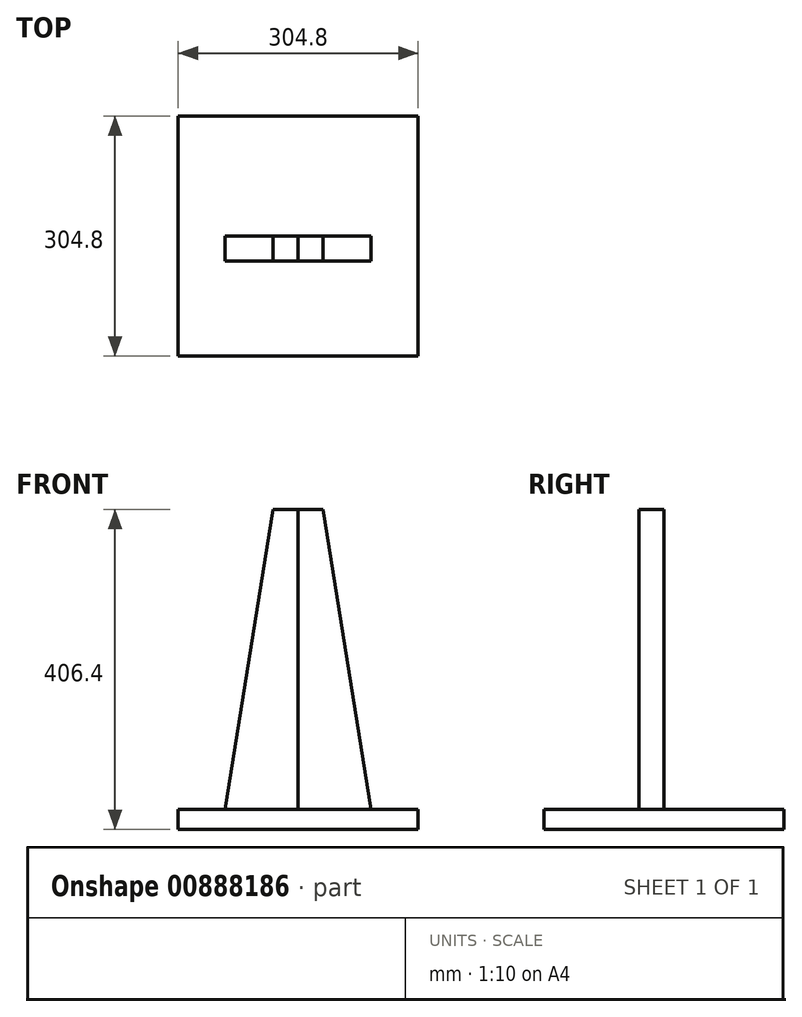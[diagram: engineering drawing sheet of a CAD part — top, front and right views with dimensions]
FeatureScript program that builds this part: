
annotation { "Feature Type Name" : "Feature", "Feature Type Description" : "" }
export const myFeature = defineFeature(function(context is Context, id is Id, definition is map)
    precondition{}
    {
        {
            var Q0;
            Q0=qCreatedBy(makeId("Top.planeOp"),FACE);
            var sketch = newSketch(context, id + "F0", { "sketchPlane" : qUnion([Q0])});
            skLineSegment(sketch, "E0.bottom", {"start": v(152.4, 152.4) * mm, "end": v(-152.4, 152.4) * mm});
            skLineSegment(sketch, "E0.top", {"start": v(152.4, -152.4) * mm, "end": v(-152.4, -152.4) * mm});
            skLineSegment(sketch, "E0.left", {"start": v(152.4, 152.4) * mm, "end": v(152.4, -152.4) * mm});
            skLineSegment(sketch, "E0.right", {"start": v(-152.4, 152.4) * mm, "end": v(-152.4, -152.4) * mm});
            skPoint(sketch, "E0.middle", {"position": v(0, 0) * mm});
            skSolve(sketch);
        }
        {
            var Q0;
            Q0 = qSketchRegion(id + "F0", true);
            extrude(context, id + "F1", {"entities" : qUnion([Q0]), "depth" : 25.4 * mm, "offsetDistance" : 25.4 * mm});
        }
        {
            var Q0;
            Q0=qCreatedBy(makeId("Front.planeOp"),FACE);
            var sketch = newSketch(context, id + "F2", { "sketchPlane" : qUnion([Q0])});
            skLineSegment(sketch, "E1", {"start": v(-92.74, 25.4) * mm, "end": v(-31.78, 406.4) * mm});
            skLineSegment(sketch, "E2", {"start": v(-31.78, 406.4) * mm, "end": v(0, 406.4) * mm});
            skLineSegment(sketch, "E3", {"start": v(0, 406.4) * mm, "end": v(-0.15, 25.4) * mm});
            skLineSegment(sketch, "E4", {"start": v(-0.15, 25.4) * mm, "end": v(-92.74, 25.4) * mm});
            skSolve(sketch);
        }
        {
            var Q0;
            Q0=qCreatedBy(makeId("Front.planeOp"),FACE);
            var sketch = newSketch(context, id + "F3", { "sketchPlane" : qUnion([Q0])});
            skLineSegment(sketch, "E5", {"start": v(92.44, 25.4) * mm, "end": v(31.48, 406.4) * mm});
            skLineSegment(sketch, "E6", {"start": v(-0.3, 406.4) * mm, "end": v(31.48, 406.4) * mm});
            skLineSegment(sketch, "E7", {"start": v(-0.3, 406.4) * mm, "end": v(-0.15, 25.4) * mm});
            skLineSegment(sketch, "E8", {"start": v(92.44, 25.4) * mm, "end": v(-0.15, 25.4) * mm});
            skSolve(sketch);
        }
        {
            var Q0;
            Q0=makeQuery(id+"F3.imprint","IMPRINT",FACE,{"disambiguationData":[TD([[makeQuery(id+"F3.imprint","IMPRINT",EDGE,{"derivedFrom":sQuery(id+"F3.wireOp",EDGE,"E5")}),1.0]])]});
            var Q1;
            Q1=makeQuery(id+"F2.imprint","IMPRINT",FACE,{"disambiguationData":[TD([[makeQuery(id+"F2.imprint","IMPRINT",EDGE,{"derivedFrom":sQuery(id+"F2.wireOp",EDGE,"E1")}),-1.0]])]});
            extrude(context, id + "F4", {"entities" : qUnion([Q0, Q1]), "depth" : 31.75 * mm, "offsetDistance" : 25.4 * mm});
        }
    });
